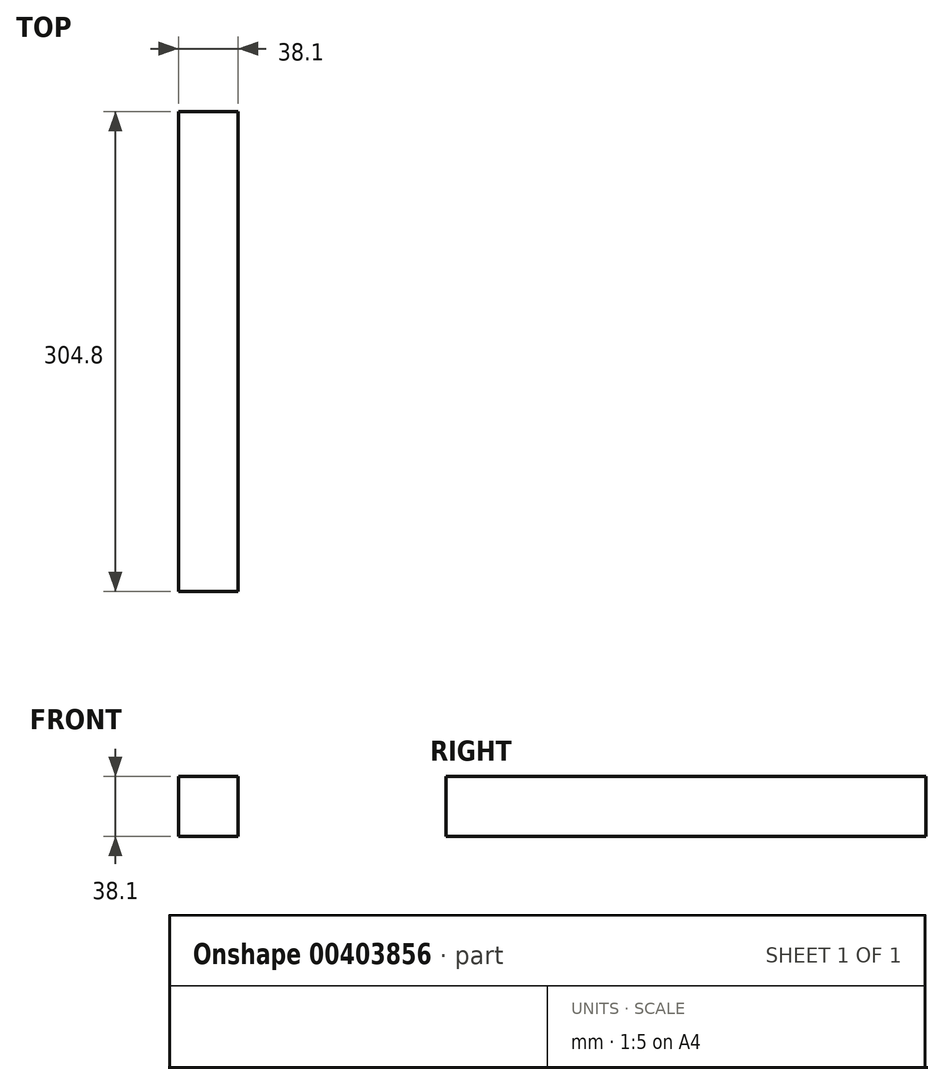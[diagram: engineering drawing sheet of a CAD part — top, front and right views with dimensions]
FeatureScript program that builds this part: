
annotation { "Feature Type Name" : "Feature", "Feature Type Description" : "" }
export const myFeature = defineFeature(function(context is Context, id is Id, definition is map)
    precondition{}
    {
        {
            var Q0;
            Q0=qCreatedBy(makeId("Front.planeOp"),FACE);
            var sketch = newSketch(context, id + "F0", { "sketchPlane" : qUnion([Q0])});
            skLineSegment(sketch, "E0.bottom", {"start": v(0, 0) * mm, "end": v(38.1, 0) * mm});
            skLineSegment(sketch, "E0.top", {"start": v(0, 38.1) * mm, "end": v(38.1, 38.1) * mm});
            skLineSegment(sketch, "E0.left", {"start": v(0, 0) * mm, "end": v(0, 38.1) * mm});
            skLineSegment(sketch, "E0.right", {"start": v(38.1, 0) * mm, "end": v(38.1, 38.1) * mm});
            skSolve(sketch);
        }
        {
            var Q0;
            Q0=makeQuery(id+"F0.imprint","IMPRINT",FACE,{"disambiguationData":[TD([[makeQuery(id+"F0.imprint","IMPRINT",EDGE,{"derivedFrom":sQuery(id+"F0.wireOp",EDGE,"E0.bottom")}),1.0]])]});
            extrude(context, id + "F1", {"entities" : qUnion([Q0]), "oppositeDirection" : true, "depth" : 304.8 * mm});
        }
    });
